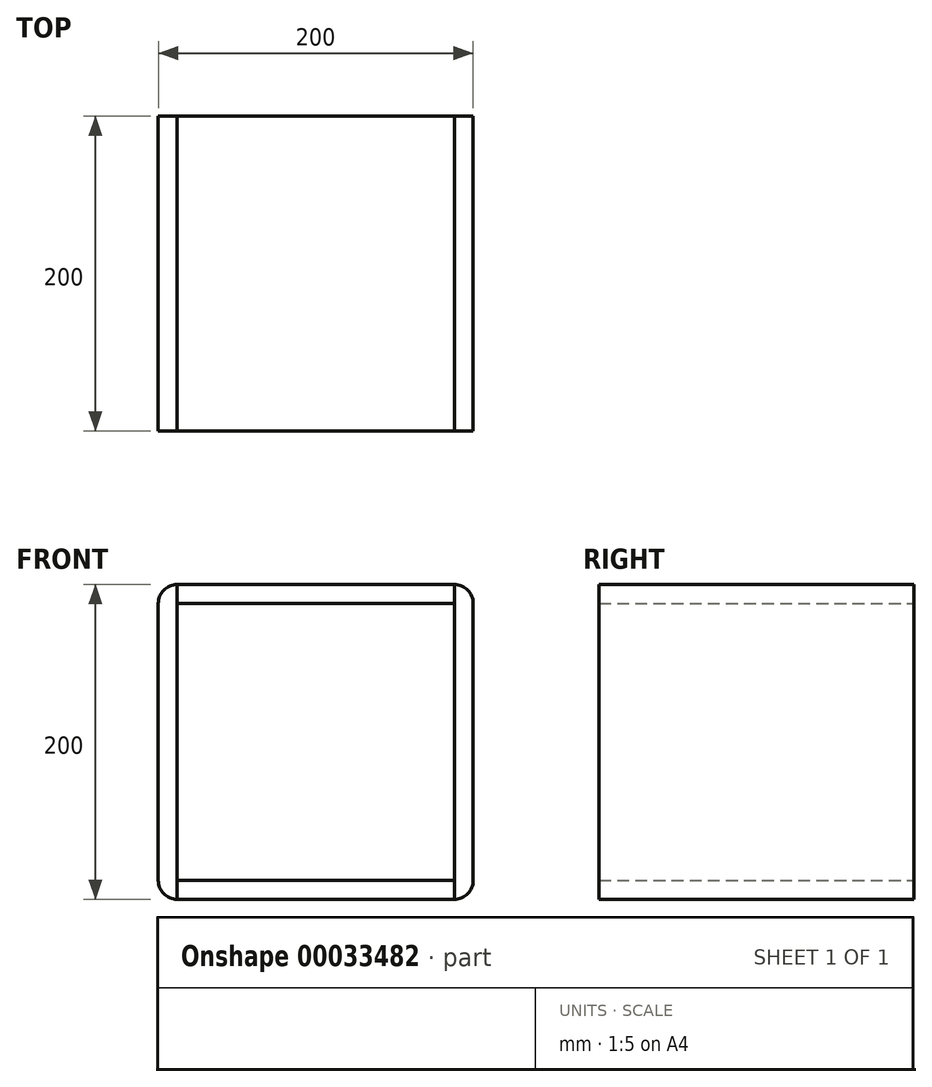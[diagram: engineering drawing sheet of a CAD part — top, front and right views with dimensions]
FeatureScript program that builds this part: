
annotation { "Feature Type Name" : "Feature", "Feature Type Description" : "" }
export const myFeature = defineFeature(function(context is Context, id is Id, definition is map)
    precondition{}
    {
        {
            assignVariable(context, id + "F0", {"name" : "MDF", "anyValue" : 12});
        }
        {
            var Q0;
            Q0=qCreatedBy(makeId("Front.planeOp"),FACE);
            var sketch = newSketch(context, id + "F1", { "sketchPlane" : qUnion([Q0])});
            skLineSegment(sketch, "E0.bottom", {"start": v(-49.46, 97.15) * mm, "end": v(-37.46, 97.15) * mm});
            skLineSegment(sketch, "E0.top", {"start": v(-49.46, -102.85) * mm, "end": v(-37.46, -102.85) * mm});
            skLineSegment(sketch, "E0.left", {"start": v(-49.46, 97.15) * mm, "end": v(-49.46, -102.85) * mm});
            skLineSegment(sketch, "E0.right", {"start": v(-37.46, 97.15) * mm, "end": v(-37.46, -90.85) * mm});
            skLineSegment(sketch, "E1.bottom", {"start": v(-37.46, 97.15) * mm, "end": v(138.54, 97.15) * mm});
            skLineSegment(sketch, "E1.top", {"start": v(-37.46, 85.15) * mm, "end": v(138.54, 85.15) * mm});
            skLineSegment(sketch, "E1.left", {"start": v(-37.46, 97.15) * mm, "end": v(-37.46, 85.15) * mm});
            skLineSegment(sketch, "E1.right", {"start": v(138.54, 97.15) * mm, "end": v(138.54, 85.15) * mm});
            skLineSegment(sketch, "E2.bottom", {"start": v(138.54, 97.15) * mm, "end": v(150.54, 97.15) * mm});
            skLineSegment(sketch, "E2.top", {"start": v(138.54, -102.85) * mm, "end": v(150.54, -102.85) * mm});
            skLineSegment(sketch, "E2.left", {"start": v(138.54, 97.15) * mm, "end": v(138.54, -102.85) * mm});
            skLineSegment(sketch, "E2.right", {"start": v(150.54, 97.15) * mm, "end": v(150.54, -102.85) * mm});
            skLineSegment(sketch, "E3.bottom", {"start": v(-37.46, -90.85) * mm, "end": v(138.54, -90.85) * mm});
            skLineSegment(sketch, "E3.top", {"start": v(-37.46, -102.85) * mm, "end": v(138.54, -102.85) * mm});
            skLineSegment(sketch, "E3.left", {"start": v(-37.46, -90.85) * mm, "end": v(-37.46, -102.85) * mm});
            skLineSegment(sketch, "E3.right", {"start": v(138.54, -90.85) * mm, "end": v(138.54, -102.85) * mm});
            skSolve(sketch);
        }
        {
            var Q0;
            Q0=makeQuery(id+"F1.imprint","IMPRINT",FACE,{"disambiguationData":[TD([[makeQuery(id+"F1.imprint","IMPRINT",EDGE,{"derivedFrom":sQuery(id+"F1.wireOp",EDGE,"E0.bottom")}),-1.0]])]});
            var Q1;
            {var subQ3=sQuery(id+"F1.wireOp",EDGE,"E2.bottom");Q1=makeQuery(id+"F1.imprint","IMPRINT",FACE,{"disambiguationData":[TD([[makeQuery(id+"F1.imprint","IMPRINT",EDGE,{"derivedFrom":subQ3}),-1.0]])]});}
            extrude(context, id + "F2", {"entities" : qUnion([Q0, Q1]), "depth" : 200 * mm});
        }
        {
            var Q0;
            {var subQ2=sQuery(id+"F1.wireOp",EDGE,"E1.bottom");Q0=makeQuery(id+"F1.imprint","IMPRINT",FACE,{"disambiguationData":[TD([[makeQuery(id+"F1.imprint","IMPRINT",EDGE,{"derivedFrom":subQ2}),-1.0]])]});}
            var Q1;
            Q1=makeQuery(id+"F1.imprint","IMPRINT",FACE,{"disambiguationData":[TD([[makeQuery(id+"F1.imprint","IMPRINT",EDGE,{"derivedFrom":sQuery(id+"F1.wireOp",EDGE,"E3.bottom")}),-1.0]])]});
            extrude(context, id + "F3", {"entities" : qUnion([Q0, Q1]), "depth" : 200 * mm});
        }
        {
            var Q0;
            Q0=makeQuery(id+"F2.opExtrude","SWEPT_EDGE",EDGE,{"disambiguationData":[OSD([sQuery(id+"F1.wireOp",EDGE,"E2.top"),sQuery(id+"F1.wireOp",EDGE,"E2.right")])]});
            var Q1;
            Q1=makeQuery(id+"F2.opExtrude","SWEPT_EDGE",EDGE,{"disambiguationData":[OSD([sQuery(id+"F1.wireOp",EDGE,"E0.top"),sQuery(id+"F1.wireOp",EDGE,"E0.left")])]});
            var Q2;
            Q2=makeQuery(id+"F2.opExtrude","SWEPT_EDGE",EDGE,{"disambiguationData":[OSD([sQuery(id+"F1.wireOp",EDGE,"E0.bottom"),sQuery(id+"F1.wireOp",EDGE,"E0.left")])]});
            var Q3;
            Q3=makeQuery(id+"F2.opExtrude","SWEPT_EDGE",EDGE,{"disambiguationData":[OSD([sQuery(id+"F1.wireOp",EDGE,"E2.bottom"),sQuery(id+"F1.wireOp",EDGE,"E2.right")])]});
            fillet(context, id + "F4", {"entities" : qUnion([Q0, Q1, Q2, Q3]), "radius" : (getVariable(context, 'MDF')) * mm, "tangentPropagation" : true, "allowEdgeOverflow" : false});
        }
    });
